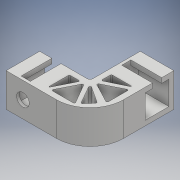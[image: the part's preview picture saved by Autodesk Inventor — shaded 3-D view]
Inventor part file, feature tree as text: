
AUTODESK INVENTOR PART (.ipt)
format: ipt  version: 2017 (Build 210142000, 142)  size: 248,832 bytes
history: native  units: mm
features: extrude x4, fillet x4, sketch x4, hole x2
ambient origin geometry x8: Origin, YZ Plane, XZ Plane, XY Plane, X Axis, Y Axis, Z Axis, Center Point
bodies: Solid1 (feature_tree)
feature tree (14):
  extrude  "Extrusion1"  Depth=60.0mm
  extrude  "Extrusion2"  Depth=60.0mm
  extrude  "Extrusion4"  Depth=150.0mm
  hole  "Hole2"  [1 undecoded]
  hole  "Hole4"  [1 undecoded]
  fillet  "Fillet1"  Radius=42.5mm
  fillet  "Fillet2"  Radius=42.5mm
  extrude  "Extrusion5"  Depth=55.0mm TaperAngle=0.0deg
  fillet  "Fillet3"  Radius=84.852814mm
  fillet  "Fillet4"  [1 undecoded]
  sketch  "Sketch1"  dims[d5=90.0mm d6=60.0mm]
  sketch  "Sketch2"  dims[d7=90.0mm d9=60.0mm]
  sketch  "Sketch4"  dims[d10=150.0mm d11=150.0mm]
  sketch  "Sketch5"  dims[d12=60.0mm d13=0.0mm d14=84.852814mm d15=45.0deg d16=42.5mm d17=42.5mm d18=55.0mm d19=0.0mm d26=84.852814mm d27=135.0deg d28=42.5mm d29=42.5mm d30=55.0mm d31=0.0mm d32=8.25mm d33=8.25mm d34=90.0deg d35=8.25mm d36=8.25mm d37=90.0deg d47=21.25mm d48=21.25mm d49=22.5mm d50=6.0mm d51=4.0mm d52=2.0mm d53=90.0deg d54=8.0mm d55=20.594885mm d65=21.25mm d66=21.25mm d67=22.5mm d68=6.0mm d69=4.0mm d70=2.0mm d71=90.0deg d72=8.0mm d73=20.594885mm d74=5.0mm d75=60.0mm d76=60.0mm d77=60.0mm d78=60.0mm d79=60.0mm d80=60.0mm d81=10.0mm d82=10.0mm d83=60.0mm d84=10.0mm d85=10.0mm d86=10.0mm d87=80.0mm d88=10.0mm d89=10.0mm d90=10.0mm d91=10.0mm d92=10.0mm d93=10.0mm d94=10.0mm d95=94.0mm d96=0.0mm d97=7.0mm d98=2.0mm d99=1.0mm]
note: 3 required parameter values undecoded (feature->parameter linkage not recoverable at this tier; creation-order binding heuristic only, values carry confidence <= 0.55)
